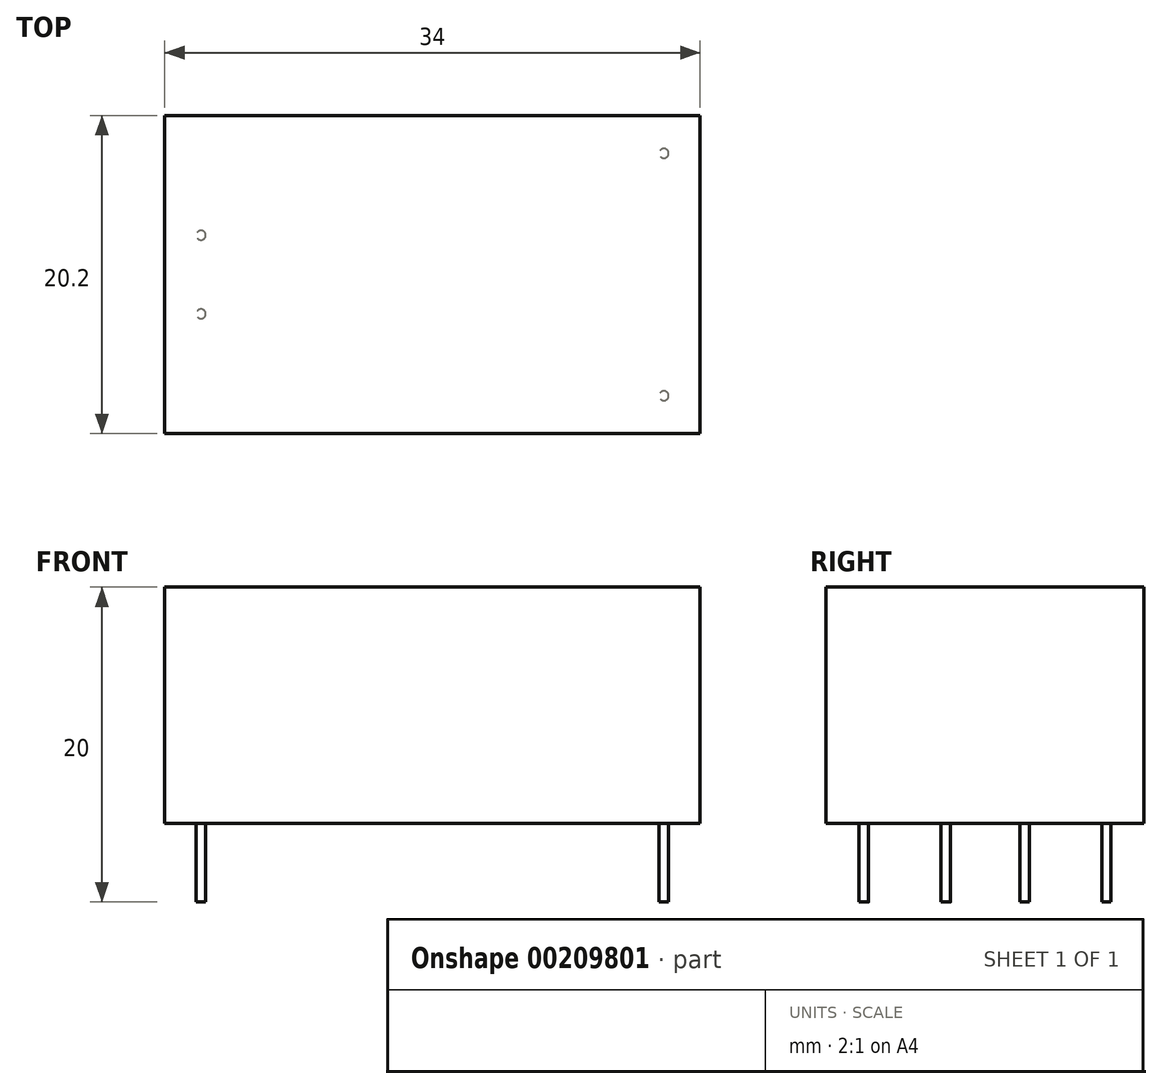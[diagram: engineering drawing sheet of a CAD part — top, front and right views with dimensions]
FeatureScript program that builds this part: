
annotation { "Feature Type Name" : "Feature", "Feature Type Description" : "" }
export const myFeature = defineFeature(function(context is Context, id is Id, definition is map)
    precondition{}
    {
        {
            var Q0;
            Q0=qCreatedBy(makeId("Top.planeOp"),FACE);
            var sketch = newSketch(context, id + "F0", { "sketchPlane" : qUnion([Q0]) });
            skLineSegment(sketch, "E0.bottom", {"start": v(-17, 10.1) * mm, "end": v(17, 10.1) * mm});
            skLineSegment(sketch, "E0.top", {"start": v(-17, -10.1) * mm, "end": v(17, -10.1) * mm});
            skLineSegment(sketch, "E0.left", {"start": v(-17, 10.1) * mm, "end": v(-17, -10.1) * mm});
            skLineSegment(sketch, "E0.right", {"start": v(17, 10.1) * mm, "end": v(17, -10.1) * mm});
            skCircle(sketch, "E1", {"center": v(-14.7, 2.5) * mm, "radius": 0.3 * mm});
            skCircle(sketch, "E2", {"center": v(-14.7, -2.5) * mm, "radius": 0.3 * mm});
            skCircle(sketch, "E3", {"center": v(14.7, 7.7) * mm, "radius": 0.3 * mm});
            skCircle(sketch, "E4", {"center": v(14.7, -7.7) * mm, "radius": 0.3 * mm});
            skLineSegment(sketch, "E5", {"start": v(-14.7, 2.5) * mm, "end": v(-14.7, -2.5) * mm, "construction": true});
            skLineSegment(sketch, "E6", {"start": v(14.7, 7.7) * mm, "end": v(14.7, -7.7) * mm, "construction": true});
            skSolve(sketch);
        }
        {
            var Q0;
            Q0=makeQuery(id+"F0.imprint","IMPRINT",FACE,{"disambiguationData":[TD([[makeQuery(id+"F0.imprint","IMPRINT",EDGE,{"derivedFrom":sQuery(id+"F0.wireOp",EDGE,"E1")}),1.0]])]});
            var Q1;
            Q1=makeQuery(id+"F0.imprint","IMPRINT",FACE,{"disambiguationData":[TD([[makeQuery(id+"F0.imprint","IMPRINT",EDGE,{"derivedFrom":sQuery(id+"F0.wireOp",EDGE,"E0.bottom")}),-1.0]])]});
            var Q2;
            Q2=makeQuery(id+"F0.imprint","IMPRINT",FACE,{"disambiguationData":[TD([[makeQuery(id+"F0.imprint","IMPRINT",EDGE,{"derivedFrom":sQuery(id+"F0.wireOp",EDGE,"E3")}),1.0]])]});
            var Q3;
            Q3=makeQuery(id+"F0.imprint","IMPRINT",FACE,{"disambiguationData":[TD([[makeQuery(id+"F0.imprint","IMPRINT",EDGE,{"derivedFrom":sQuery(id+"F0.wireOp",EDGE,"E4")}),1.0]])]});
            var Q4;
            Q4=makeQuery(id+"F0.imprint","IMPRINT",FACE,{"disambiguationData":[TD([[makeQuery(id+"F0.imprint","IMPRINT",EDGE,{"derivedFrom":sQuery(id+"F0.wireOp",EDGE,"E2")}),1.0]])]});
            extrude(context, id + "F1", {"entities" : qUnion([Q0, Q1, Q2, Q3, Q4]), "depth" : 15 * mm});
        }
        {
            var Q0;
            Q0=makeQuery(id+"F0.imprint","IMPRINT",FACE,{"disambiguationData":[TD([[makeQuery(id+"F0.imprint","IMPRINT",EDGE,{"derivedFrom":sQuery(id+"F0.wireOp",EDGE,"E2")}),1.0]])]});
            var Q1;
            Q1=makeQuery(id+"F0.imprint","IMPRINT",FACE,{"disambiguationData":[TD([[makeQuery(id+"F0.imprint","IMPRINT",EDGE,{"derivedFrom":sQuery(id+"F0.wireOp",EDGE,"E1")}),1.0]])]});
            var Q2;
            Q2=makeQuery(id+"F0.imprint","IMPRINT",FACE,{"disambiguationData":[TD([[makeQuery(id+"F0.imprint","IMPRINT",EDGE,{"derivedFrom":sQuery(id+"F0.wireOp",EDGE,"E4")}),1.0]])]});
            var Q3;
            Q3=makeQuery(id+"F0.imprint","IMPRINT",FACE,{"disambiguationData":[TD([[makeQuery(id+"F0.imprint","IMPRINT",EDGE,{"derivedFrom":sQuery(id+"F0.wireOp",EDGE,"E3")}),1.0]])]});
            extrude(context, id + "F2", {"entities" : qUnion([Q0, Q1, Q2, Q3]), "oppositeDirection" : true, "depth" : 5 * mm});
        }
    });
